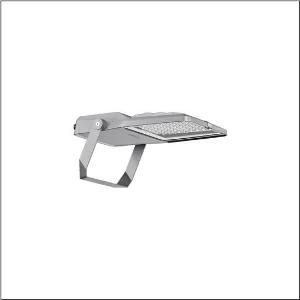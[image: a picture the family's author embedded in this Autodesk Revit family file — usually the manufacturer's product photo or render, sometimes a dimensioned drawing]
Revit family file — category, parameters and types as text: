
# Revit family: floodlight_fl_21_iq_mini___pl43_5xa7772b1a1a_21a9
name_source: partatom
category: Lighting Fixtures
units: mm (PartAtom-declared; Revit-internal decimal feet)

## family parameters
Cut with Voids When Loaded = No
Host = Face
Light Source = No
Part Type = Normal
Room Calculation Point = No
Round Connector Dimension = Use Diameter
Shared = No

## types (1)
- --- (1 x LED, 5300 lm, 45.5 W, 2200K)
    Apparent Load = 46 VA
    CIE Flux Codes = 27 78 99 100 100
    Color Rendering = 70
    Color Temperature = 2200K
    Default Elevation = 1800 mm
    Description = Floodlight FL 21 iQ mini, floodlight, primary light control with lens, of PMMA, primary optical cover: protective disc, of toughened safety glass, transparent, light distribution: PL43, light emission: direct distribution, installation type: surface-mounted, LED, High Power LED, rated luminous flux: 5.300lm, luminous efficacy: 117lm/W, light colour: 722, colour temperature: 2200K, control: Street-Remote, Auto-Match, Temp-Guard, Night-Set, Smart-Wire, Desk-Remote (wireless, voltage-free reading and setting of iQ features in the workshop via application-optimized NFC function/RFID function), optimised constant luminous flux control (CLO 2.0), with terminal, 6-pole, mains connection: 220..240V, AC, 50/60Hz, start of lifetime: 46W, end of service life: 48W, reduction: 21W, luminaire housing, of diecast aluminium, powder-coated, Siteco® metallic grey (DB 702S), corrosivity category C5 mid according to DIN EN ISO 12944, sealing non-destructively replaceable, mounting bracket, of steel, galvanised, powder-coated, Siteco® metallic grey (DB 702S), protection rating (complete): IP66, insulation class (complete): insulation class II (safety insulation), certification: CE, ENEC, VDE, protection symbol: D, impact resistance: IK08, permissible operating ambient temperature: -40..+40°C, permissible operating ambient temperature for outdoor applications: -40..+50°C, standard: DIN EN 12944, LABS conformity tested according to VDMA 24364:2018-05, packaging unit: 1 piece

Light Distribution: PL43
    Height = 70 mm
    Lamp = 1 x LED
    Lamp Light Flux = 5300 lm
    Lamp Power = 45.5 W
    Lamp count = 1
    Length = 485 mm
    Luminous efficacy = 116 lm/W
    Manufacturer = Siteco
    ModVariant = No
    Model = 5XA7772B1A1A
    Number of Poles = 1
    OnlyDefault = Yes
    Power Factor = 1
    Product Name = Floodlight FL 21 iQ mini | PL43
    Product group = floodlight | pylon annexe
    ProductGroupID = 6200
    Protection Class = Protection class II
    Protection Degree = IP 66
    RLX_Detail_Level = 1
    RLX_Emergency_Light_Flux = 0 lm
    RLX_Emergency_Type = 0
    RLX_Emergency_Type_DB = No
    RlxData = <blob elided: 96105 chars, md5=5a4f086b>
    Socket = socket
    Standby Power = 0 W
    System Light Flux = 5300 lm
    System Power = 46 W
    Type Comments = factory setting: luminous flux: 100 % | dim-lin: 254 | 463 mA
    Type Image = l_1006845.jpg
    URL = http://relux.com
    VarID = @adj_113013
    Voltage = 0 V
    Weight = 0.00 kg
    Width = 337 mm

## geometry (parser evidence)
native form markers: Blend x4, Sweep x10
no freeform markers — native parametric forms only
